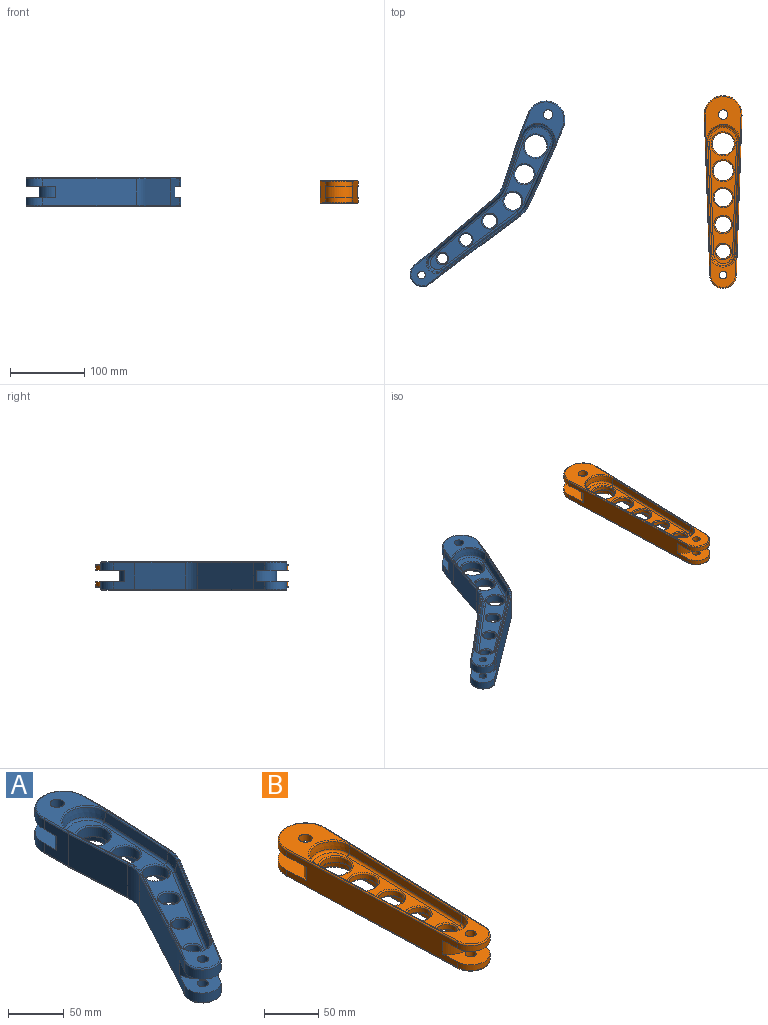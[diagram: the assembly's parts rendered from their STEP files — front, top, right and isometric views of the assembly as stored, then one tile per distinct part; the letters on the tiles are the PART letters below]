
ASSEMBLY  parts=2 mates=2
PART A: 115 faces, bbox 123.6x300.1x38.1 mm
  f0: plane 35.56x22mm, normal (-0.87,0.5,0), area 637.1mm2, adj f1,f6,f7,f21,f25,f108,f109,f110
  f1: cylinder r=16.74mm len=27.87mm, axis (0,0,-1), area 474mm2, adj f0,f2,f100,f109
  f2: plane 133.81x82.3mm, normal (0.85,-0.52,0), area 5255.5mm2, adj f1,f21,f28,f91,f98,f108,f109,f110
  f3: plane 35.56x30.48mm, normal (-1,0,0), area 844.6mm2, adj f5,f8,f10,f23,f24,f105,f106,f107
  f4: plane 35.56x30.48mm, normal (1,0,0), area 844.6mm2, adj f5,f9,f11,f22,f23,f105,f106,f107
  f5: cylinder r=25.43mm len=50.87mm, axis (0,0,-1), area 838.9mm2, adj f3,f4,f101,f106
  f6: extruded ~22.59x13.82mm, area 50.7mm2, adj f0,f26,f93,f95
  f7: extruded ~22.59x13.82mm, area 50.7mm2, adj f0,f27,f100,f102
  f8: extruded ~30.55x1.27mm, area 60.8mm2, adj f3,f26,f92,f94
  f9: extruded ~30.55x1.27mm, area 60.8mm2, adj f4,f26,f90,f92
  f10: extruded ~30.55x1.27mm, area 60.8mm2, adj f3,f27,f101,f103
  f11: extruded ~30.55x1.27mm, area 60.8mm2, adj f4,f27,f99,f101
  f12: plane 109.06x67.96mm, normal (-0.84,0.52,-0.17), area 1231.7mm2, adj f13,f19,f45,f80
  f13: cone r=33.02mm half-angle=10deg, axis (0,0,-1), area 165.7mm2, adj f12,f14,f43,f79
  f14: plane 83.43x9.55mm, normal (-0.98,0.05,-0.17), area 809.4mm2, adj f13,f15,f41,f77
  f15: cone r=20.35mm half-angle=10deg, axis (0,0,-1), area 679.1mm2, adj f14,f16,f39,f75
  f16: plane 71.41x9.55mm, normal (0.98,0.05,-0.17), area 692.7mm2, adj f15,f17,f40,f73
  f17: cone r=43.18mm half-angle=10deg, axis (0,0,1), area 220.2mm2, adj f16,f18,f42,f74
  f18: plane 102.35x55.49mm, normal (0.87,-0.46,-0.17), area 1115.6mm2, adj f17,f19,f44,f76
  f19: cone r=11.66mm half-angle=10deg, axis (0,0,-1), area 383.3mm2, adj f12,f18,f46,f78
  f20: plane 229.7x93.04mm, normal (0,0,-1), area 3558.6mm2, adj f39,f40,f41,f42,f43,f44,f45,f46
  f21: cylinder r=16.74mm len=27.87mm, axis (0,0,-1), area 474mm2, adj f0,f2,f93,f110
  f22: plane 83.34x35.56mm, normal (1,-0.05,0), area 2967.6mm2, adj f4,f28,f90,f99
  f23: cylinder r=25.43mm len=50.87mm, axis (0,0,-1), area 838.9mm2, adj f3,f4,f92,f107
  f24: plane 71.33x35.56mm, normal (-1,-0.05,0), area 2539.8mm2, adj f3,f29,f94,f103
  f25: plane 101.56x54mm, normal (-0.88,0.47,0), area 4090.2mm2, adj f0,f29,f95,f102
  f26: plane 294.06x117.62mm, normal (0,0,1), area 2320.7mm2, adj f6,f8,f9,f81,f82,f83,f84,f85
  f27: plane 294.06x117.62mm, normal (0,0,-1), area 2320.7mm2, adj f7,f10,f11,f73,f74,f75,f76,f77
  f28: cylinder r=38.1mm len=35.56mm, axis (0,0,1), area 676.1mm2, adj f2,f22,f89,f97
  f29: cylinder r=38.1mm len=35.56mm, axis (0,0,1), area 733mm2, adj f24,f25,f96,f104
  f30: plane 109.06x67.96mm, normal (-0.84,0.52,0.17), area 1231.7mm2, adj f31,f37,f51,f85
  f31: cone r=33.02mm half-angle=10deg, axis (0,0,1), area 165.7mm2, adj f30,f32,f49,f83
  f32: plane 83.43x9.55mm, normal (-0.98,0.05,0.17), area 809.4mm2, adj f31,f33,f47,f81
  f33: cone r=20.35mm half-angle=10deg, axis (0,0,1), area 679.1mm2, adj f32,f34,f48,f82
  f34: plane 71.41x9.55mm, normal (0.98,0.05,0.17), area 692.7mm2, adj f33,f35,f50,f84
  f35: cone r=43.18mm half-angle=10deg, axis (0,0,-1), area 220.2mm2, adj f34,f36,f52,f86
  f36: plane 102.35x55.49mm, normal (0.87,-0.46,0.17), area 1115.6mm2, adj f35,f37,f54,f88
  f37: cone r=11.66mm half-angle=10deg, axis (0,0,1), area 383.3mm2, adj f30,f36,f53,f87
  f38: plane 229.7x93.04mm, normal (0,0,1), area 3558.6mm2, adj f47,f48,f49,f50,f51,f52,f53,f54
  f39: torus R=18.22mm, axis (0,0,-1), area 227.1mm2, adj f15,f20,f40,f41
  f40: cylinder r=2.54mm len=71.46mm, axis (-0.05,1,0), area 253.3mm2, adj f16,f20,f39,f42
  f41: cylinder r=2.54mm len=83.47mm, axis (-0.05,-1,0), area 296mm2, adj f14,f20,f39,f43
  f42: torus R=45.31mm, axis (0,0,-1), area 84.1mm2, adj f17,f20,f40,f44
  f43: torus R=30.89mm, axis (0,0,-1), area 57.3mm2, adj f13,f20,f41,f45
  f44: cylinder r=2.54mm len=102.73mm, axis (0.47,0.88,0), area 407.9mm2, adj f18,f20,f42,f46
  f45: cylinder r=2.54mm len=109.48mm, axis (-0.52,-0.85,0), area 450.4mm2, adj f12,f20,f43,f46
  f46: torus R=9.52mm, axis (0,0,-1), area 120.1mm2, adj f19,f20,f44,f45
  f47: cylinder r=2.54mm len=83.47mm, axis (-0.05,-1,0), area 296mm2, adj f32,f38,f48,f49
  f48: torus R=18.22mm, axis (0,0,1), area 227.1mm2, adj f33,f38,f47,f50
  f49: torus R=30.89mm, axis (0,0,1), area 57.3mm2, adj f31,f38,f47,f51
  f50: cylinder r=2.54mm len=71.46mm, axis (-0.05,1,0), area 253.3mm2, adj f34,f38,f48,f52
  f51: cylinder r=2.54mm len=109.48mm, axis (-0.52,-0.85,0), area 450.4mm2, adj f30,f38,f49,f53
  f52: torus R=45.31mm, axis (0,0,1), area 84.1mm2, adj f35,f38,f50,f54
  f53: torus R=9.52mm, axis (0,0,1), area 120.1mm2, adj f37,f38,f51,f54
  f54: cylinder r=2.54mm len=102.73mm, axis (0.47,0.88,0), area 407.9mm2, adj f36,f38,f52,f53
  f55: cylinder r=7.23mm len=14.45mm, axis (0,0,1), area 461.2mm2, adj f66,f67
  f56: cylinder r=8.35mm len=16.71mm, axis (0,0,1), area 533.3mm2, adj f65,f68
  f57: cylinder r=9.48mm len=18.97mm, axis (0,0,1), area 605.4mm2, adj f64,f69
  f58: cylinder r=12.17mm len=24.34mm, axis (0,0,1), area 776.9mm2, adj f63,f70
  f59: cylinder r=13.16mm len=26.32mm, axis (0,0,1), area 840.1mm2, adj f62,f71
  f60: cylinder r=15.29mm len=30.57mm, axis (0,0,1), area 975.9mm2, adj f61,f72
  f61: torus R=16.56mm, axis (0,0,-1), area 197.4mm2, adj f20,f60
  f62: torus R=14.43mm, axis (0,0,-1), area 170.7mm2, adj f20,f59
  f63: torus R=13.44mm, axis (0,0,-1), area 158.3mm2, adj f20,f58
  f64: torus R=10.75mm, axis (0,0,-1), area 124.7mm2, adj f20,f57
  f65: torus R=9.62mm, axis (0,0,-1), area 110.5mm2, adj f20,f56
  f66: torus R=8.5mm, axis (0,0,-1), area 96.3mm2, adj f20,f55
  f67: torus R=8.5mm, axis (0,0,1), area 96.3mm2, adj f38,f55
  f68: torus R=9.62mm, axis (0,0,1), area 110.5mm2, adj f38,f56
  f69: torus R=10.75mm, axis (0,0,1), area 124.7mm2, adj f38,f57
  f70: torus R=13.44mm, axis (0,0,1), area 158.3mm2, adj f38,f58
  f71: torus R=14.43mm, axis (0,0,1), area 170.7mm2, adj f38,f59
  f72: torus R=16.56mm, axis (0,0,1), area 197.4mm2, adj f38,f60
  f73: cylinder r=1.27mm len=71.39mm, axis (-0.05,1,0), area 126.7mm2, adj f16,f27,f74,f75
  f74: torus R=39.87mm, axis (0,0,1), area 39mm2, adj f17,f27,f73,f76
  f75: torus R=23.66mm, axis (0,0,1), area 131.9mm2, adj f15,f27,f73,f77
  f76: cylinder r=1.27mm len=102.15mm, axis (0.47,0.88,0), area 204mm2, adj f18,f27,f74,f78
  f77: cylinder r=1.27mm len=83.4mm, axis (-0.05,-1,0), area 148mm2, adj f14,f27,f75,f79
  f78: torus R=14.96mm, axis (0,0,1), area 77.4mm2, adj f19,f27,f76,f80
  f79: torus R=36.33mm, axis (0,0,1), area 31.5mm2, adj f13,f27,f77,f80
  f80: cylinder r=1.27mm len=108.84mm, axis (-0.52,-0.85,0), area 225.2mm2, adj f12,f27,f78,f79
  f81: cylinder r=1.27mm len=83.4mm, axis (0.05,1,0), area 148mm2, adj f26,f32,f82,f83
  f82: torus R=23.66mm, axis (0,0,1), area 131.9mm2, adj f26,f33,f81,f84
  f83: torus R=36.33mm, axis (0,0,1), area 31.5mm2, adj f26,f31,f81,f85
  f84: cylinder r=1.27mm len=71.39mm, axis (0.05,-1,0), area 126.7mm2, adj f26,f34,f82,f86
  f85: cylinder r=1.27mm len=108.84mm, axis (0.52,0.85,0), area 225.2mm2, adj f26,f30,f83,f87
  f86: torus R=39.87mm, axis (0,0,1), area 39mm2, adj f26,f35,f84,f88
  f87: torus R=14.96mm, axis (0,0,1), area 77.4mm2, adj f26,f37,f85,f88
  f88: cylinder r=1.27mm len=102.15mm, axis (-0.47,-0.88,0), area 204mm2, adj f26,f36,f86,f87
  f89: torus R=36.83mm, axis (0,0,1), area 37.5mm2, adj f26,f28,f90,f91
  f90: cylinder r=1.27mm len=83.4mm, axis (-0.05,-1,0), area 166.5mm2, adj f9,f22,f26,f89
  f91: cylinder r=1.27mm len=134.48mm, axis (-0.52,-0.85,0), area 313.2mm2, adj f2,f26,f89,f93
  f92: torus R=24.16mm, axis (0,0,1), area 161.7mm2, adj f8,f9,f23,f26
  f93: torus R=15.47mm, axis (0,0,1), area 90.3mm2, adj f6,f21,f26,f91
  f94: cylinder r=1.27mm len=71.39mm, axis (-0.05,1,0), area 142.5mm2, adj f8,f24,f26,f96
  f95: cylinder r=1.27mm len=102.16mm, axis (0.47,0.88,0), area 229.5mm2, adj f6,f25,f26,f96
  f96: torus R=39.37mm, axis (0,0,1), area 41.6mm2, adj f26,f29,f94,f95
  f97: torus R=36.83mm, axis (0,0,1), area 37.5mm2, adj f27,f28,f98,f99
  f98: cylinder r=1.27mm len=134.48mm, axis (0.52,0.85,0), area 313.2mm2, adj f2,f27,f97,f100
  f99: cylinder r=1.27mm len=83.4mm, axis (0.05,1,0), area 166.5mm2, adj f11,f22,f27,f97
  f100: torus R=15.47mm, axis (0,0,1), area 90.3mm2, adj f1,f7,f27,f98
  f101: torus R=24.16mm, axis (0,0,1), area 161.7mm2, adj f5,f10,f11,f27
  f102: cylinder r=1.27mm len=102.16mm, axis (-0.47,-0.88,0), area 229.5mm2, adj f7,f25,f27,f104
  f103: cylinder r=1.27mm len=71.39mm, axis (0.05,-1,0), area 142.5mm2, adj f10,f24,f27,f104
  f104: torus R=39.37mm, axis (0,0,1), area 41.6mm2, adj f27,f29,f102,f103
  f105: cylinder r=28.74mm len=50.8mm, axis (0,0,1), area 949.5mm2, adj f3,f4,f106,f107
  f106: plane 50.87x42.47mm, normal (0,0,1), area 1201.1mm2, adj f3,f4,f5,f105,f114
  f107: plane 50.87x42.47mm, normal (0,0,-1), area 1201.1mm2, adj f3,f4,f23,f105,f113
  f108: cylinder r=18.77mm len=28.57mm, axis (0,0,1), area 621.5mm2, adj f0,f2,f109,f110
  f109: plane 39.72x39.24mm, normal (0,0,1), area 668.4mm2, adj f0,f1,f2,f108,f112
  f110: plane 39.72x39.24mm, normal (0,0,-1), area 668.4mm2, adj f0,f2,f21,f108,f111
  f111: cylinder r=5.08mm len=11.43mm, axis (0,0,1), area 364.8mm2, adj f26,f110
  f112: cylinder r=5.08mm len=11.43mm, axis (0,0,1), area 364.8mm2, adj f27,f109
  f113: cylinder r=6.35mm len=12.7mm, axis (0,0,1), area 456mm2, adj f26,f107
  f114: cylinder r=6.35mm len=12.7mm, axis (0,0,1), area 456mm2, adj f27,f106
PART B: 67 faces, bbox 55x262.8x30.5 mm
  f0: plane 215.64x27.94mm, normal (1,-0.03,0), area 5370mm2, adj f1,f5,f12,f15,f27,f28,f29,f30
  f1: cylinder r=25.42mm len=50.83mm, axis (0,0,-1), area 518.3mm2, adj f0,f2,f31,f42
  f2: plane 215.64x27.94mm, normal (-1,-0.03,0), area 5370mm2, adj f1,f5,f12,f15,f27,f28,f29,f30
  f3: cylinder r=6.35mm len=12.7mm, axis (0,0,-1), area 304mm2, adj f16,f31
  f4: cylinder r=5.08mm len=10.16mm, axis (0,0,-1), area 243.2mm2, adj f16,f28
  f5: cylinder r=17.88mm len=35.74mm, axis (0,0,-1), area 348.8mm2, adj f0,f2,f28,f43
  f6: plane 152.24x7.95mm, normal (-1,0.03,-0.09), area 1215.8mm2, adj f7,f9,f36,f52
  f7: cone r=20.36mm half-angle=5deg, axis (0,0,-1), area 536.2mm2, adj f6,f8,f34,f50
  f8: plane 152.24x7.95mm, normal (1,0.03,-0.09), area 1215.8mm2, adj f7,f9,f33,f49
  f9: cone r=15.05mm half-angle=5deg, axis (0,0,-1), area 382.4mm2, adj f6,f8,f35,f51
  f10: plane 183.16x36.07mm, normal (0,0,-1), area 2488.9mm2, adj f49,f50,f51,f52,f57,f59,f61,f63
  f11: plane 256.66x48.29mm, normal (0,0,1), area 2623.9mm2, adj f13,f14,f37,f38,f39,f40,f45,f46
  f12: cylinder r=25.42mm len=50.83mm, axis (0,0,-1), area 518.3mm2, adj f0,f2,f32,f46
  f13: cylinder r=6.35mm len=12.7mm, axis (0,0,-1), area 304mm2, adj f11,f32
  f14: cylinder r=5.08mm len=10.16mm, axis (0,0,-1), area 243.2mm2, adj f11,f29
  f15: cylinder r=17.88mm len=35.74mm, axis (0,0,-1), area 348.8mm2, adj f0,f2,f29,f47
  f16: plane 256.66x48.29mm, normal (0,0,-1), area 2623.9mm2, adj f3,f4,f33,f34,f35,f36,f41,f42
  f17: plane 152.24x7.95mm, normal (-1,0.03,0.09), area 1215.8mm2, adj f18,f20,f40,f56
  f18: cone r=20.36mm half-angle=5deg, axis (0,0,1), area 536.2mm2, adj f17,f19,f38,f54
  f19: plane 152.24x7.95mm, normal (1,0.03,0.09), area 1215.8mm2, adj f18,f20,f37,f53
  f20: cone r=15.05mm half-angle=5deg, axis (0,0,1), area 382.4mm2, adj f17,f19,f39,f55
  f21: plane 183.16x36.07mm, normal (0,0,1), area 2488.9mm2, adj f53,f54,f55,f56,f58,f60,f62,f64
  f22: cylinder r=9.83mm len=19.66mm, axis (0,0,1), area 313.7mm2, adj f65,f66
  f23: cylinder r=11.09mm len=22.18mm, axis (0,0,1), area 354mm2, adj f63,f64
  f24: cylinder r=12.36mm len=24.71mm, axis (0,0,1), area 394.4mm2, adj f61,f62
  f25: cylinder r=13.62mm len=27.24mm, axis (0,0,1), area 434.7mm2, adj f59,f60
  f26: cylinder r=14.88mm len=29.76mm, axis (0,0,1), area 475mm2, adj f57,f58
  f27: cylinder r=21.13mm len=37.02mm, axis (0,0,1), area 687.7mm2, adj f0,f2,f28,f29
  f28: plane 37.02x35.64mm, normal (0,0,1), area 779.5mm2, adj f0,f2,f4,f5,f27
  f29: plane 37.02x35.64mm, normal (0,0,-1), area 779.5mm2, adj f0,f2,f14,f15,f27
  f30: cylinder r=26.44mm len=49.07mm, axis (0,0,1), area 957.8mm2, adj f0,f2,f31,f32
  f31: plane 51.11x50.83mm, normal (0,0,1), area 1582.7mm2, adj f0,f1,f2,f3,f30
  f32: plane 51.11x50.83mm, normal (0,0,-1), area 1582.7mm2, adj f0,f2,f12,f13,f30
  f33: cylinder r=1.27mm len=152.26mm, axis (-0.03,1,0), area 287mm2, adj f8,f16,f34,f35
  f34: torus R=22.53mm, axis (0,0,1), area 131.6mm2, adj f7,f16,f33,f36
  f35: torus R=17.21mm, axis (0,0,1), area 95.1mm2, adj f9,f16,f33,f36
  f36: cylinder r=1.27mm len=152.26mm, axis (0.03,1,0), area 287mm2, adj f6,f16,f34,f35
  f37: cylinder r=1.27mm len=152.26mm, axis (0.03,-1,0), area 287mm2, adj f11,f19,f38,f39
  f38: torus R=22.53mm, axis (0,0,1), area 131.6mm2, adj f11,f18,f37,f40
  f39: torus R=17.21mm, axis (0,0,1), area 95.1mm2, adj f11,f20,f37,f40
  f40: cylinder r=1.27mm len=152.26mm, axis (-0.03,-1,0), area 287mm2, adj f11,f17,f38,f39
  f41: cylinder r=1.27mm len=215.68mm, axis (0.03,-1,0), area 430.4mm2, adj f2,f16,f42,f43
  f42: torus R=24.15mm, axis (0,0,1), area 159.9mm2, adj f1,f16,f41,f44
  f43: torus R=16.61mm, axis (0,0,1), area 106.7mm2, adj f5,f16,f41,f44
  f44: cylinder r=1.27mm len=215.68mm, axis (0.03,1,0), area 430.4mm2, adj f0,f16,f42,f43
  f45: cylinder r=1.27mm len=215.68mm, axis (-0.03,1,0), area 430.4mm2, adj f2,f11,f46,f47
  f46: torus R=24.15mm, axis (0,0,1), area 159.9mm2, adj f11,f12,f45,f48
  f47: torus R=16.61mm, axis (0,0,1), area 106.7mm2, adj f11,f15,f45,f48
  f48: cylinder r=1.27mm len=215.68mm, axis (-0.03,-1,0), area 430.4mm2, adj f0,f11,f46,f47
  f49: cylinder r=2.54mm len=152.3mm, axis (-0.03,1,0), area 573.9mm2, adj f8,f10,f50,f51
  f50: torus R=18.04mm, axis (0,0,-1), area 237.2mm2, adj f7,f10,f49,f52
  f51: torus R=12.72mm, axis (0,0,-1), area 165.3mm2, adj f9,f10,f49,f52
  f52: cylinder r=2.54mm len=152.3mm, axis (0.03,1,0), area 573.9mm2, adj f6,f10,f50,f51
  f53: cylinder r=2.54mm len=152.3mm, axis (-0.03,1,0), area 573.9mm2, adj f19,f21,f54,f55
  f54: torus R=18.04mm, axis (0,0,1), area 237.2mm2, adj f18,f21,f53,f56
  f55: torus R=12.72mm, axis (0,0,1), area 165.3mm2, adj f20,f21,f53,f56
  f56: cylinder r=2.54mm len=152.3mm, axis (0.03,1,0), area 573.9mm2, adj f17,f21,f54,f55
  f57: torus R=16.15mm, axis (0,0,-1), area 192.3mm2, adj f10,f26
  f58: torus R=16.15mm, axis (0,0,1), area 192.3mm2, adj f21,f26
  f59: torus R=14.89mm, axis (0,0,-1), area 176.5mm2, adj f10,f25
  f60: torus R=14.89mm, axis (0,0,1), area 176.5mm2, adj f21,f25
  f61: torus R=13.63mm, axis (0,0,-1), area 160.6mm2, adj f10,f24
  f62: torus R=13.63mm, axis (0,0,1), area 160.6mm2, adj f21,f24
  f63: torus R=12.36mm, axis (0,0,-1), area 144.8mm2, adj f10,f23
  f64: torus R=12.36mm, axis (0,0,1), area 144.8mm2, adj f21,f23
  f65: torus R=11.1mm, axis (0,0,-1), area 129mm2, adj f10,f22
  f66: torus R=11.1mm, axis (0,0,1), area 129mm2, adj f21,f22
PLACE A rot(axis=(0,0,-1),21.6deg) t=(-60.73,-46.36,0)mm
PLACE B t=(221.53,-36.23,0)mm
MATE pin_slot A.f111 <-> B.f4  axis (0,0,1) through (-184.15,-144.18,-7.62)mm
MATE pin_slot A.f113 <-> B.f1  axis (0,0,1) through (-13.98,71.72,-7.62)mm
